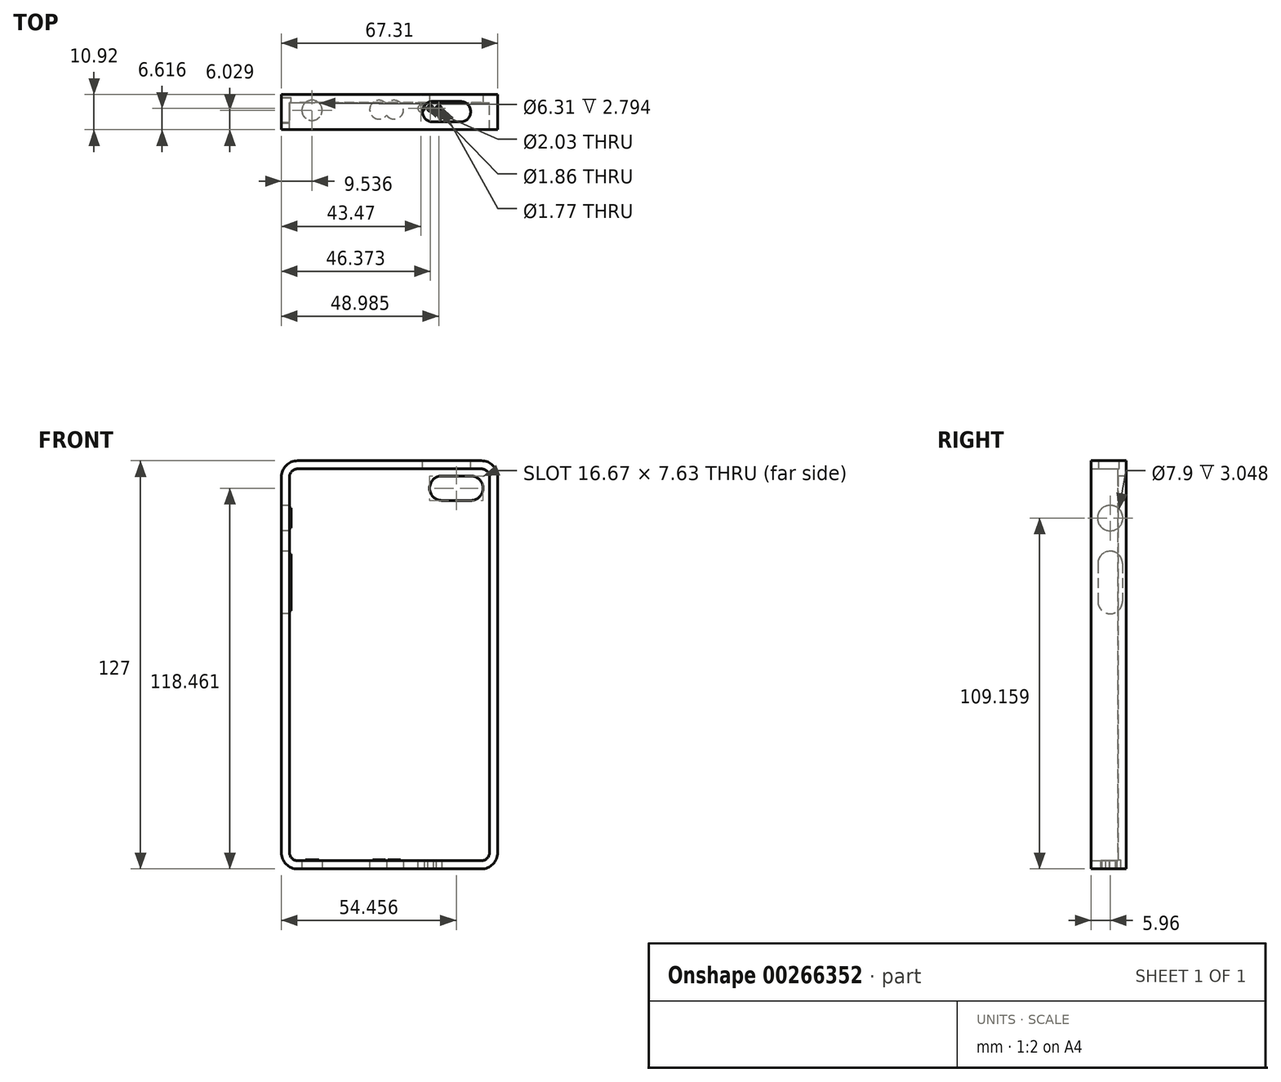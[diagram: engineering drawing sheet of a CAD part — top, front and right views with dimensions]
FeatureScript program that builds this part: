
annotation { "Feature Type Name" : "Feature", "Feature Type Description" : "" }
export const myFeature = defineFeature(function(context is Context, id is Id, definition is map)
    precondition{}
    {
        {
            var Q0;
            Q0=qCreatedBy(makeId("Front.planeOp"),FACE);
            var sketch = newSketch(context, id + "F0", { "sketchPlane" : qUnion([Q0])});
            skLineSegment(sketch, "E0", {"start": v(0, 89.38) * mm, "end": v(-35.1, 89.38) * mm});
            skLineSegment(sketch, "E1", {"start": v(-35.1, 89.38) * mm, "end": v(-35.1, -37.62) * mm});
            skLineSegment(sketch, "E2", {"start": v(-35.1, -37.62) * mm, "end": v(32.21, -37.62) * mm});
            skLineSegment(sketch, "E3", {"start": v(32.21, -37.62) * mm, "end": v(32.21, 89.38) * mm});
            skLineSegment(sketch, "E4", {"start": v(32.21, 89.38) * mm, "end": v(0, 89.38) * mm});
            skSolve(sketch);
        }
        {
            var Q0;
            Q0 = qSketchRegion(id + "F0", true);
            extrude(context, id + "F1", {"entities" : qUnion([Q0]), "depth" : 10.92 * mm});
        }
        {
            var Q0;
            Q0=makeQuery(id+"F1.opExtrude","SWEPT_EDGE",EDGE,{"disambiguationData":[OSD([sQuery(id+"F0.wireOp",EDGE,"E0"),sQuery(id+"F0.wireOp",EDGE,"E1")])]});
            var Q1;
            Q1=makeQuery(id+"F1.opExtrude","SWEPT_EDGE",EDGE,{"disambiguationData":[OSD([sQuery(id+"F0.wireOp",EDGE,"E3"),sQuery(id+"F0.wireOp",EDGE,"E4")])]});
            var Q2;
            Q2=makeQuery(id+"F1.opExtrude","SWEPT_EDGE",EDGE,{"disambiguationData":[OSD([sQuery(id+"F0.wireOp",EDGE,"E2"),sQuery(id+"F0.wireOp",EDGE,"E3")])]});
            var Q3;
            Q3=makeQuery(id+"F1.opExtrude","SWEPT_EDGE",EDGE,{"disambiguationData":[OSD([sQuery(id+"F0.wireOp",EDGE,"E1"),sQuery(id+"F0.wireOp",EDGE,"E2")])]});
            fillet(context, id + "F2", {"entities" : qUnion([Q0, Q1, Q2, Q3]), "radius" : 5.08 * mm, "tangentPropagation" : true, "allowEdgeOverflow" : false});
        }
        {
            var Q0;
            Q0=makeQuery(id+"F1.opExtrude","CAP_FACE",FACE,{"disambiguationData":[OSD([sQuery(id+"F0.wireOp",EDGE,"E0"),sQuery(id+"F0.wireOp",EDGE,"E1"),sQuery(id+"F0.wireOp",EDGE,"E2"),sQuery(id+"F0.wireOp",EDGE,"E3"),sQuery(id+"F0.wireOp",EDGE,"E4"),sQuery(id+"F0.wireOp",EDGE,"OJDM7tP3-sl7A-XVUf-Gswy-c9hWXv5GrE7C")])],"isStart":false});
            shell(context, id + "F3", {"entities" : qUnion([Q0]), "thickness" : 2.54 * mm});
        }
        {
            var Q0;
            Q0=makeQuery(id+"F3.opShell","OFFSET_FACE",FACE,{"disambiguationData":[OSD([sQuery(id+"F0.wireOp",EDGE,"E0"),sQuery(id+"F0.wireOp",EDGE,"E1"),sQuery(id+"F0.wireOp",EDGE,"E2"),sQuery(id+"F0.wireOp",EDGE,"E3"),sQuery(id+"F0.wireOp",EDGE,"E4")])]});
            var sketch = newSketch(context, id + "F4", { "sketchPlane" : qUnion([Q0])});
            skCircle(sketch, "E5", {"center": v(14.83, 80.84) * mm, "radius": 3.81 * mm});
            skCircle(sketch, "E6", {"center": v(23.88, 80.84) * mm, "radius": 3.81 * mm});
            skLineSegment(sketch, "E7", {"start": v(14.83, 84.65) * mm, "end": v(23.88, 84.65) * mm});
            skLineSegment(sketch, "E8", {"start": v(14.83, 77.03) * mm, "end": v(23.88, 77.03) * mm});
            skSolve(sketch);
        }
        {
            var Q0;
            Q0=makeQuery(id+"F1.opExtrude","SWEPT_FACE",FACE,{"disambiguationData":[OSD([sQuery(id+"F0.wireOp",EDGE,"E2")])]});
            var sketch = newSketch(context, id + "F5", { "sketchPlane" : qUnion([Q0])});
            skCircle(sketch, "E9", {"center": v(13.89, 4.3) * mm, "radius": 0.88 * mm});
            skCircle(sketch, "E10", {"center": v(11.27, 4.3) * mm, "radius": 0.93 * mm});
            skCircle(sketch, "E11", {"center": v(8.37, 4.3) * mm, "radius": 1.02 * mm});
            skCircle(sketch, "E12", {"center": v(-4.7, 4.7) * mm, "radius": 2.92 * mm});
            skCircle(sketch, "E13", {"center": v(0, 4.7) * mm, "radius": 2.92 * mm});
            skCircle(sketch, "E14", {"center": v(-25.56, 4.9) * mm, "radius": 3.15 * mm});
            skSolve(sketch);
        }
        {
            var Q0;
            Q0 = qSketchRegion(id + "F5", true);
            extrude(context, id + "F6", {"entities" : qUnion([Q0]), "operationType" : NewBodyOperationType.REMOVE, "oppositeDirection" : true, "depth" : 2.8 * mm});
        }
        {
            var Q0;
            Q0=makeQuery(id+"F1.opExtrude","SWEPT_FACE",FACE,{"disambiguationData":[OSD([sQuery(id+"F0.wireOp",EDGE,"E1")])]});
            var sketch = newSketch(context, id + "F7", { "sketchPlane" : qUnion([Q0])});
            skCircle(sketch, "E15", {"center": v(4.96, 71.54) * mm, "radius": 3.95 * mm});
            skCircle(sketch, "E16", {"center": v(4.96, 57.43) * mm, "radius": 3.81 * mm});
            skCircle(sketch, "E17", {"center": v(4.96, 45.6) * mm, "radius": 3.81 * mm});
            skLineSegment(sketch, "E18", {"start": v(8.77, 57.43) * mm, "end": v(8.77, 45.6) * mm});
            skLineSegment(sketch, "E19", {"start": v(1.15, 57.43) * mm, "end": v(1.15, 45.6) * mm});
            skSolve(sketch);
        }
        {
            var Q0;
            Q0 = qSketchRegion(id + "F7", true);
            extrude(context, id + "F8", {"entities" : qUnion([Q0]), "operationType" : NewBodyOperationType.REMOVE, "oppositeDirection" : true, "depth" : 3.05 * mm});
        }
        {
            var Q0;
            Q0=makeQuery(id+"F1.opExtrude","SWEPT_FACE",FACE,{"disambiguationData":[OSD([sQuery(id+"F0.wireOp",EDGE,"E0"),sQuery(id+"F0.wireOp",EDGE,"E4")])]});
            var sketch = newSketch(context, id + "F9", { "sketchPlane" : qUnion([Q0])});
            skCircle(sketch, "E20", {"center": v(20.64, -5.33) * mm, "radius": 3.18 * mm});
            skCircle(sketch, "E21", {"center": v(11.97, -5.33) * mm, "radius": 3.18 * mm});
            skLineSegment(sketch, "E22", {"start": v(11.97, -2.16) * mm, "end": v(20.64, -2.16) * mm});
            skLineSegment(sketch, "E23", {"start": v(11.97, -8.5) * mm, "end": v(20.64, -8.5) * mm});
            skSolve(sketch);
        }
        {
            var Q0;
            Q0 = qSketchRegion(id + "F9", true);
            extrude(context, id + "F10", {"entities" : qUnion([Q0]), "operationType" : NewBodyOperationType.REMOVE, "oppositeDirection" : true, "depth" : 2.54 * mm});
        }
        {
            var Q0;
            Q0 = qSketchRegion(id + "F4", true);
            extrude(context, id + "F11", {"entities" : qUnion([Q0]), "operationType" : NewBodyOperationType.ADD, "depth" : 25.4 * mm});
        }
        {
            var Q0;
            Q0 = qSketchRegion(id + "F4", true);
            extrude(context, id + "F12", {"entities" : qUnion([Q0]), "operationType" : NewBodyOperationType.REMOVE, "depth" : 42.42 * mm});
        }
        {
            var Q0;
            Q0 = qSketchRegion(id + "F4", true);
            extrude(context, id + "F13", {"entities" : qUnion([Q0]), "operationType" : NewBodyOperationType.REMOVE, "oppositeDirection" : true, "depth" : 25.4 * mm});
        }
        {
            var Q0;
            Q0 = qSketchRegion(id + "F9", true);
            extrude(context, id + "F14", {"entities" : qUnion([Q0]), "operationType" : NewBodyOperationType.REMOVE, "oppositeDirection" : true, "depth" : 2.54 * mm});
        }
    });
